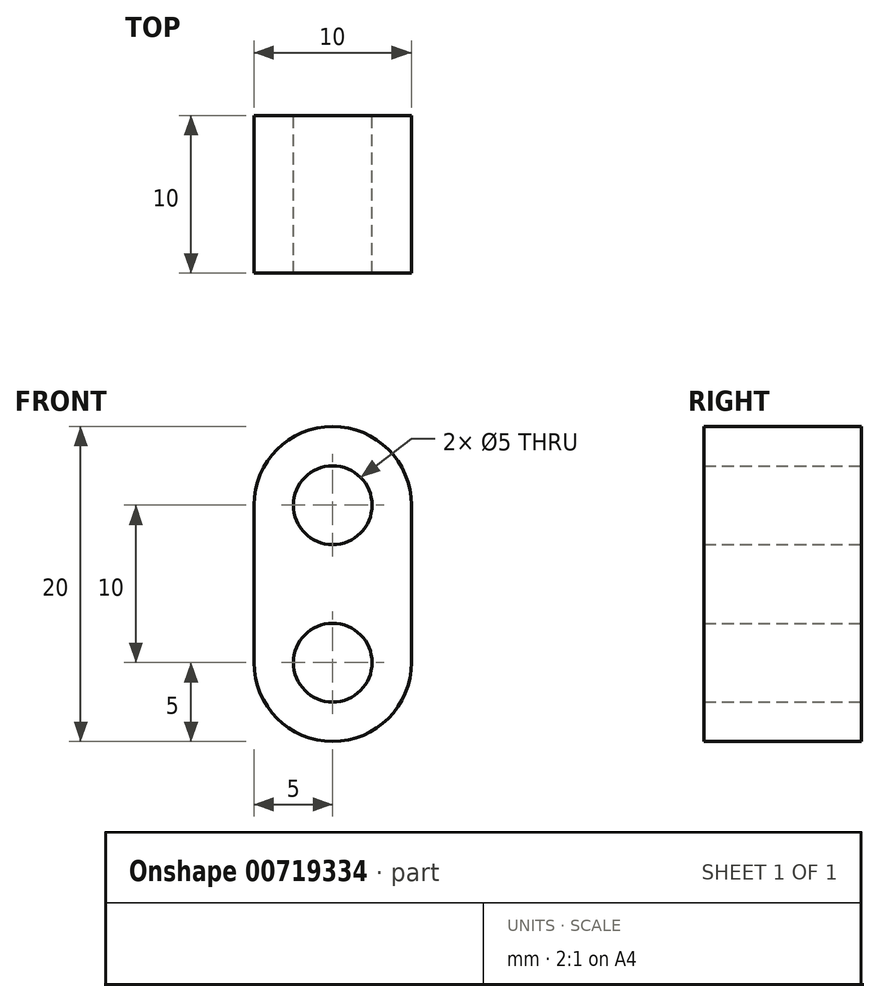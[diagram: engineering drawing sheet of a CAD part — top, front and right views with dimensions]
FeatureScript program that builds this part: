
annotation { "Feature Type Name" : "Feature", "Feature Type Description" : "" }
export const myFeature = defineFeature(function(context is Context, id is Id, definition is map)
    precondition{}
    {
        {
            var Q0;
            Q0=qCreatedBy(makeId("Front.planeOp"),FACE);
            var sketch = newSketch(context, id + "F0", { "sketchPlane" : qUnion([Q0])});
            skCircle(sketch, "E0", {"center": v(0, 0) * mm, "radius": 2.5 * mm});
            skArc(sketch, "E1", {"start": v(5, 0) * mm, "mid": v(0, 5) * mm, "end": v(-5, 0) * mm});
            skCircle(sketch, "E2", {"center": v(0, -10) * mm, "radius": 2.5 * mm});
            skArc(sketch, "E3", {"start": v(-5, -10) * mm, "mid": v(0, -15) * mm, "end": v(5, -10) * mm});
            skLineSegment(sketch, "E4", {"start": v(-5, 0) * mm, "end": v(-5, -10) * mm});
            skLineSegment(sketch, "E5", {"start": v(5, 0) * mm, "end": v(5, -10) * mm});
            skSolve(sketch);
        }
        {
            var Q0;
            Q0=makeQuery(id+"F0.imprint","IMPRINT",FACE,{"disambiguationData":[TD([[makeQuery(id+"F0.imprint","IMPRINT",EDGE,{"derivedFrom":sQuery(id+"F0.wireOp",EDGE,"E0")}),-1.0]])]});
            extrude(context, id + "F1", {"entities" : qUnion([Q0]), "depth" : 10 * mm, "offsetDistance" : 25 * mm});
        }
    });
